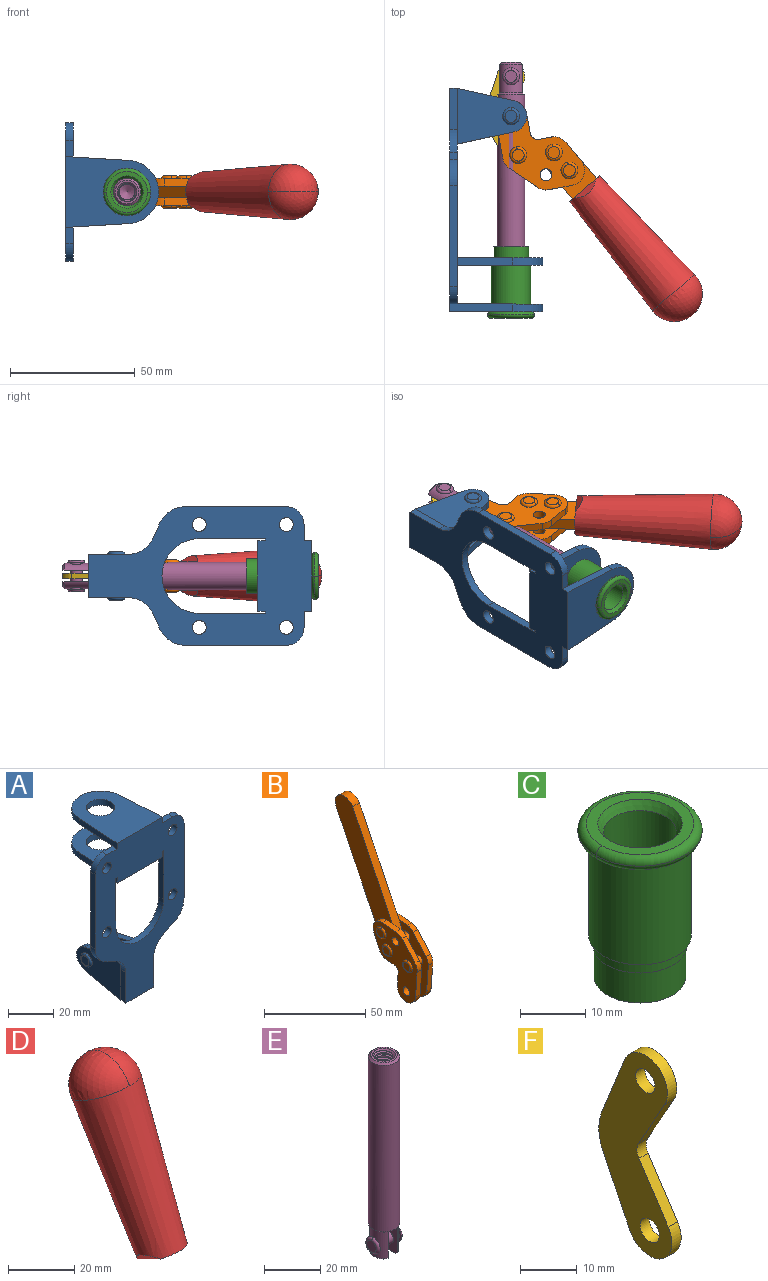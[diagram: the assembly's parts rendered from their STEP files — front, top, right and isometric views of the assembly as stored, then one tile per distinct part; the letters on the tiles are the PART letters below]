
ASSEMBLY  parts=6 mates=6
PART A: 55 faces, bbox 55.7x37.4x89.8 mm
  f0: torus R=2.41mm, axis (-1,0,0), area 15mm2, adj f11,f15,f25
  f1: torus R=2.41mm, axis (-1,0,0), area 15mm2, adj f10,f12,f22
  f2: cylinder r=2.78mm len=5.56mm, axis (0,-1,0), area 54.2mm2, adj f30,f54
  f3: cylinder r=14.99mm len=29.97mm, axis (0,-1,0), area 145.9mm2, adj f30,f49,f53,f54
  f4: cylinder r=2.78mm len=5.56mm, axis (0,-1,0), area 54.2mm2, adj f30,f54
  f5: cylinder r=2.78mm len=5.56mm, axis (0,-1,0), area 54.2mm2, adj f30,f54
  f6: cylinder r=2.78mm len=5.56mm, axis (0,-1,0), area 54.2mm2, adj f30,f54
  f7: cylinder r=6.35mm len=12.7mm, axis (0,0,1), area 123.6mm2, adj f27,f51
  f8: cylinder r=6.35mm len=12.7mm, axis (0,0,-1), area 124.7mm2, adj f21,f35
  f9: cylinder r=2.41mm len=11.18mm, axis (-1,0,0), area 169.4mm2, adj f16,f19
  f10: plane 4.83x4.83mm, normal (1,0,0), area 18.3mm2, adj f1,f12
  f11: plane 4.83x4.83mm, normal (-1,0,0), area 18.3mm2, adj f0,f15
  f12: torus R=2.41mm, axis (-1,0,0), area 15mm2, adj f1,f10,f22
  f13: cylinder r=6.35mm len=12.41mm, axis (1,0,0), area 53.4mm2, adj f18,f19,f22,f23
  f14: cylinder r=6.35mm len=12.41mm, axis (-1,0,0), area 53.4mm2, adj f16,f17,f24,f25
  f15: torus R=2.41mm, axis (-1,0,0), area 15mm2, adj f0,f11,f25
  f16: plane 27.86x22.35mm, normal (1,0,0), area 425.4mm2, adj f9,f14,f17,f24,f30
  f17: plane 22.86x4.97mm, normal (0,0.21,0.98), area 72.5mm2, adj f14,f16,f25,f30
  f18: plane 22.86x4.97mm, normal (0,0.21,0.98), area 72.5mm2, adj f13,f19,f22,f30
  f19: plane 27.86x22.35mm, normal (-1,0,0), area 425.4mm2, adj f9,f13,f18,f23,f30
  f20: cylinder r=12.7mm len=25.35mm, axis (0,0,-1), area 119.8mm2, adj f21,f34,f35,f36
  f21: plane 34.21x28.07mm, normal (0,0,-1), area 702.4mm2, adj f8,f20,f30,f34,f36
  f22: plane 27.96x22.45mm, normal (1,0,0), area 407.2mm2, adj f1,f12,f13,f18,f23,f30,f42,f43
  f23: plane 22.86x4.97mm, normal (0,0.21,-0.98), area 72.5mm2, adj f13,f19,f22,f44
  f24: plane 22.86x4.97mm, normal (0,0.21,-0.98), area 72.5mm2, adj f14,f16,f25,f44
  f25: plane 27.86x22.35mm, normal (-1,0,0), area 407.1mm2, adj f0,f14,f15,f17,f24,f30,f45,f46
  f26: plane 3.1x0.95mm, normal (0,0,-1), area 2.7mm2, adj f30,f49,f50,f54
  f27: plane 34.21x28.07mm, normal (0,0,1), area 702.4mm2, adj f7,f28,f30,f50,f52
  f28: cylinder r=12.7mm len=25.35mm, axis (0,0,1), area 118.8mm2, adj f27,f50,f51,f52
  f29: plane 3.1x0.95mm, normal (0,0,-1), area 2.7mm2, adj f30,f52,f53,f54
  f30: plane 86.54x55.63mm, normal (0,1,0), area 2362.9mm2, adj f2,f3,f4,f5,f6,f16,f17,f18
  f31: plane 40.56x3.1mm, normal (-1,0,0), area 125.7mm2, adj f30,f32,f48,f54
  f32: cylinder r=7.11mm len=7.11mm, axis (0,-1,0), area 34.6mm2, adj f30,f31,f33,f54
  f33: plane 6.67x3.1mm, normal (0,0,1), area 20.4mm2, adj f30,f32,f34,f54
  f34: plane 25.39x3.13mm, normal (-1,0.06,0), area 79.5mm2, adj f20,f21,f33,f35,f54
  f35: plane 37.31x28.45mm, normal (0,0,1), area 789.9mm2, adj f8,f20,f34,f36,f54
  f36: plane 25.39x3.13mm, normal (1,0.06,0), area 79.5mm2, adj f20,f21,f35,f37,f54
  f37: plane 6.67x3.1mm, normal (0,0,1), area 20.4mm2, adj f30,f36,f38,f54
  f38: cylinder r=7.11mm len=7.11mm, axis (0,-1,0), area 34.6mm2, adj f30,f37,f39,f54
  f39: plane 40.56x3.1mm, normal (1,0,0), area 125.7mm2, adj f30,f38,f40,f54
  f40: cylinder r=11.18mm len=10.16mm, axis (0,-1,0), area 39.5mm2, adj f30,f39,f41,f54
  f41: plane 6.09x3.1mm, normal (0.42,0,-0.91), area 20.8mm2, adj f30,f40,f42,f54
  f42: cylinder r=11.18mm len=9.41mm, axis (0,-1,0), area 37.2mm2, adj f22,f30,f41,f43,f54
  f43: plane 16.5x3.1mm, normal (1,0,0), area 51.1mm2, adj f22,f42,f44,f54
  f44: plane 17.37x3.1mm, normal (0,0,-1), area 53.8mm2, adj f23,f24,f30,f43,f45,f54
  f45: plane 16.5x3.1mm, normal (-1,0,0), area 51.1mm2, adj f25,f44,f46,f54
  f46: cylinder r=11.18mm len=9.41mm, axis (0,-1,0), area 37.2mm2, adj f25,f30,f45,f47,f54
  f47: plane 6.09x3.1mm, normal (-0.42,0,-0.91), area 20.8mm2, adj f30,f46,f48,f54
  f48: cylinder r=11.18mm len=10.16mm, axis (0,-1,0), area 39.5mm2, adj f30,f31,f47,f54
  f49: plane 26.54x3.1mm, normal (-1,0,0), area 82.3mm2, adj f3,f26,f30,f54
  f50: plane 25.39x3.1mm, normal (1,0.06,0), area 78.8mm2, adj f26,f27,f28,f51,f54
  f51: plane 37.31x28.45mm, normal (0,0,-1), area 789.9mm2, adj f7,f28,f50,f52,f54
  f52: plane 25.39x3.1mm, normal (-1,0.06,0), area 78.8mm2, adj f27,f28,f29,f51,f54
  f53: plane 26.54x3.1mm, normal (1,0,0), area 82.3mm2, adj f3,f29,f30,f54
  f54: plane 89.66x55.63mm, normal (0,-1,0), area 2678.5mm2, adj f2,f3,f4,f5,f6,f26,f29,f31
PART B: 59 faces, bbox 12.9x60.2x99.6 mm
  f0: torus R=2.39mm, axis (-1,0,0), area 14.9mm2, adj f20,f43,f51
  f1: torus R=2.39mm, axis (-1,0,0), area 14.9mm2, adj f19,f42,f51
  f2: torus R=2.39mm, axis (-1,0,0), area 14.9mm2, adj f18,f35,f51
  f3: torus R=2.39mm, axis (-1,0,0), area 14.9mm2, adj f14,f17,f23
  f4: torus R=2.39mm, axis (-1,0,0), area 14.9mm2, adj f13,f16,f23
  f5: torus R=2.39mm, axis (-1,0,0), area 14.9mm2, adj f12,f15,f23
  f6: cylinder r=2.39mm len=4.78mm, axis (1,0,0), area 46.5mm2, adj f48,f50,f51
  f7: cylinder r=2.39mm len=4.78mm, axis (1,0,0), area 46.5mm2, adj f50,f51
  f8: cylinder r=6.35mm len=12.68mm, axis (1,0,0), area 61.8mm2, adj f38,f39,f50,f51
  f9: cylinder r=2.39mm len=4.78mm, axis (-1,0,0), area 70.5mm2, adj f46,f50
  f10: cylinder r=2.39mm len=4.78mm, axis (-1,0,0), area 46.5mm2, adj f23,f45,f46
  f11: cylinder r=2.39mm len=4.78mm, axis (-1,0,0), area 46.5mm2, adj f23,f46
  f12: plane 4.78x4.78mm, normal (1,0,0), area 17.9mm2, adj f5,f15
  f13: plane 4.78x4.78mm, normal (1,0,0), area 17.9mm2, adj f4,f16
  f14: plane 4.78x4.78mm, normal (1,0,0), area 17.9mm2, adj f3,f17
  f15: torus R=2.39mm, axis (-1,0,0), area 14.9mm2, adj f5,f12,f23
  f16: torus R=2.39mm, axis (-1,0,0), area 14.9mm2, adj f4,f13,f23
  f17: torus R=2.39mm, axis (-1,0,0), area 14.9mm2, adj f3,f14,f23
  f18: plane 4.78x4.78mm, normal (-1,0,0), area 17.9mm2, adj f2,f35
  f19: plane 4.78x4.78mm, normal (-1,0,0), area 17.9mm2, adj f1,f42
  f20: plane 4.78x4.78mm, normal (-1,0,0), area 17.9mm2, adj f0,f43
  f21: plane 2.26x0.2mm, normal (1,0,0), area 0.2mm2, adj f31,f44
  f22: plane 2.26x0.2mm, normal (-1,0,0), area 0.2mm2, adj f41,f44
  f23: plane 39.37x30.77mm, normal (1,0,0), area 565.5mm2, adj f3,f4,f5,f10,f11,f15,f16,f17
  f24: cylinder r=6.1mm len=4.15mm, axis (-1,0,0), area 14.7mm2, adj f23,f25,f32,f46
  f25: plane 10.25x9.01mm, normal (0,-0.75,0.66), area 42.3mm2, adj f23,f24,f26,f46
  f26: cylinder r=6.35mm len=4.64mm, axis (-1,0,0), area 15.6mm2, adj f23,f25,f27,f46
  f27: plane 15.84x3.1mm, normal (0,-1,-0.07), area 49.2mm2, adj f23,f26,f28,f46
  f28: cylinder r=6.35mm len=12.68mm, axis (-1,0,0), area 61.8mm2, adj f23,f27,f29,f46
  f29: plane 8.11x3.1mm, normal (0,1,0.07), area 25.2mm2, adj f23,f28,f30,f46
  f30: cylinder r=3.05mm len=3.25mm, axis (-1,0,0), area 14.8mm2, adj f23,f29,f31,f46
  f31: plane 5.99x3.1mm, normal (0,0.07,-1), area 18.6mm2, adj f21,f23,f30,f44,f46
  f32: plane 9.5x3.1mm, normal (0,-0.07,1), area 29.5mm2, adj f23,f24,f33,f46,f47
  f33: cylinder r=6.1mm len=8.63mm, axis (-1,0,0), area 39.1mm2, adj f23,f32,f34,f47
  f34: plane 8.65x3.96mm, normal (0,0.91,-0.42), area 29.5mm2, adj f23,f33,f44,f47
  f35: torus R=2.39mm, axis (-1,0,0), area 14.9mm2, adj f2,f18,f51
  f36: plane 10.25x9.01mm, normal (0,-0.75,0.66), area 42.3mm2, adj f37,f49,f50,f51
  f37: cylinder r=6.35mm len=4.64mm, axis (1,0,0), area 15.6mm2, adj f36,f38,f50,f51
  f38: plane 15.84x3.1mm, normal (0,-1,-0.07), area 49.2mm2, adj f8,f37,f50,f51
  f39: plane 8.11x3.1mm, normal (0,1,0.07), area 25.2mm2, adj f8,f40,f50,f51
  f40: cylinder r=3.05mm len=3.25mm, axis (1,0,0), area 14.8mm2, adj f39,f41,f50,f51
  f41: plane 5.99x3.1mm, normal (0,0.07,-1), area 18.6mm2, adj f22,f40,f44,f50,f51
  f42: torus R=2.39mm, axis (-1,0,0), area 14.9mm2, adj f1,f19,f51
  f43: torus R=2.39mm, axis (-1,0,0), area 14.9mm2, adj f0,f20,f51
  f44: cylinder r=6.35mm len=12.12mm, axis (-1,0,0), area 128.9mm2, adj f21,f22,f23,f31,f34,f41,f46,f47
  f45: plane 2.65x1.35mm, normal (1,0,0), area 1mm2, adj f10,f55
  f46: plane 39.08x20.42mm, normal (-1,0,0), area 412.5mm2, adj f9,f10,f11,f24,f25,f26,f27,f28
  f47: plane 77.62x39.82mm, normal (1,0,0), area 850mm2, adj f32,f33,f34,f44,f53,f54,f55
  f48: plane 2.65x1.35mm, normal (-1,0,0), area 1mm2, adj f6,f55
  f49: cylinder r=6.1mm len=4.15mm, axis (1,0,0), area 14.7mm2, adj f36,f50,f51,f56
  f50: plane 39.08x20.42mm, normal (1,0,0), area 412.5mm2, adj f6,f7,f8,f9,f36,f37,f38,f39
  f51: plane 39.37x30.77mm, normal (-1,0,0), area 565.5mm2, adj f0,f1,f2,f6,f7,f8,f35,f36
  f52: plane 8.65x3.96mm, normal (0,0.91,-0.42), area 29.5mm2, adj f44,f51,f57,f58
  f53: plane 68.49x33.4mm, normal (0,0.9,-0.44), area 358.1mm2, adj f44,f47,f54,f58
  f54: cylinder r=6.35mm len=12.06mm, axis (1,0,0), area 93.7mm2, adj f47,f53,f55,f58
  f55: plane 68.49x33.4mm, normal (0,-0.9,0.44), area 358.1mm2, adj f44,f45,f46,f47,f48,f50,f54,f58
  f56: plane 9.5x3.1mm, normal (0,-0.07,1), area 29.5mm2, adj f49,f50,f51,f57,f58
  f57: cylinder r=6.1mm len=8.63mm, axis (1,0,0), area 39.1mm2, adj f51,f52,f56,f58
  f58: plane 77.62x39.82mm, normal (-1,0,0), area 850mm2, adj f44,f52,f53,f54,f55,f56,f57
PART C: 15 faces, bbox 20.6x20.6x28.7 mm
  f0: torus R=8.26mm, axis (0,0,1), area 56.8mm2, adj f1,f10,f12
  f1: torus R=8.26mm, axis (0,0,1), area 56.8mm2, adj f0,f6,f13
  f2: cylinder r=5.59mm len=25.91mm, axis (0,0,1), area 909.6mm2, adj f3,f4
  f3: cone r=6.86mm half-angle=45deg, axis (0,0,-1), area 70.2mm2, adj f2,f14
  f4: cone r=6.47mm half-angle=30deg, axis (0,0,1), area 66.7mm2, adj f2,f13
  f5: cylinder r=7.04mm len=14.07mm, axis (0,0,1), area 252.6mm2, adj f11,f14
  f6: torus R=8.26mm, axis (0,0,1), area 56.8mm2, adj f1,f12,f13
  f7: cylinder r=7.16mm len=14.33mm, axis (0,0,1), area 91.5mm2, adj f9,f11
  f8: cylinder r=7.86mm len=18.42mm, axis (0,0,1), area 909.6mm2, adj f9,f10
  f9: plane 15.72x15.72mm, normal (0,0,-1), area 33mm2, adj f7,f8
  f10: plane 16.51x16.51mm, normal (0,0,-1), area 19.9mm2, adj f0,f8,f12
  f11: plane 14.33x14.33mm, normal (0,0,-1), area 5.7mm2, adj f5,f7
  f12: torus R=8.26mm, axis (0,0,1), area 56.8mm2, adj f0,f6,f10
  f13: plane 16.51x16.51mm, normal (0,0,1), area 82.7mm2, adj f1,f4,f6
  f14: plane 14.07x14.07mm, normal (0,0,-1), area 7.8mm2, adj f3,f5
PART D: 11 faces, bbox 22.3x42.6x64.5 mm
  f0: sphere r=11.13mm, area 411.4mm2, adj f1,f8
  f1: cone r=11.11mm half-angle=3.3deg, axis (0,0.44,0.9), area 3251.8mm2, adj f0,f7,f8,f9,f10
  f2: cylinder r=6.16mm len=11.7mm, axis (1,0,0), area 89.5mm2, adj f3,f4,f5,f6
  f3: plane 60.23x36.75mm, normal (-1,0,0), area 763.6mm2, adj f2,f4,f6,f10
  f4: plane 51.37x25.05mm, normal (0,0.9,-0.44), area 264.2mm2, adj f2,f3,f5,f10
  f5: plane 60.23x36.75mm, normal (1,0,0), area 763.6mm2, adj f2,f4,f6,f10
  f6: plane 51.37x25.05mm, normal (0,-0.9,0.44), area 264.2mm2, adj f2,f3,f5,f10
  f7: plane 9.95x5.95mm, normal (0.71,-0.31,-0.64), area 25.8mm2, adj f1,f10
  f8: sphere r=11.13mm, area 411.4mm2, adj f0,f1
  f9: plane 9.95x5.95mm, normal (-0.71,-0.31,-0.64), area 25.8mm2, adj f1,f10
  f10: plane 14.27x11.38mm, normal (0,-0.44,-0.9), area 106.7mm2, adj f1,f3,f4,f5,f6,f7,f9
PART E: 48 faces, bbox 12.6x11.1x86.1 mm
  f0: torus R=2.41mm, axis (-1,0,0), area 15mm2, adj f30,f32,f34
  f1: torus R=2.41mm, axis (-1,0,0), area 15mm2, adj f29,f31,f33
  f2: cylinder r=5.54mm len=72.39mm, axis (0,0,1), area 2518.5mm2, adj f3,f4,f42,f43
  f3: cone r=5.54mm half-angle=45deg, axis (0,0,1), area 7.6mm2, adj f2,f5,f41
  f4: cone r=5.54mm half-angle=45deg, axis (0,0,-1), area 34.9mm2, adj f2,f39
  f5: cylinder r=5.08mm len=11.48mm, axis (0,0,1), area 108.3mm2, adj f3,f7,f8,f41
  f6: cylinder r=2.41mm len=4.83mm, axis (-1,0,0), area 71.2mm2, adj f40,f41
  f7: cylinder r=2.41mm len=4.83mm, axis (-1,0,0), area 7.6mm2, adj f5,f34
  f8: cone r=5.08mm half-angle=45deg, axis (0,0,1), area 10.6mm2, adj f5,f37,f41
  f9: cone r=3.98mm half-angle=45deg, axis (0,0,1), area 17.6mm2, adj f27,f39,f45,f46,f47
  f10: cylinder r=2.41mm len=4.83mm, axis (-1,0,0), area 7.6mm2, adj f33,f38
  f11: cylinder r=3.2mm len=6.4mm, axis (0,0,1), area 78.4mm2, adj f12,f28,f44,f45,f47
  f12: cylinder r=3.2mm len=6.4mm, axis (0,0,1), area 10.5mm2, adj f11,f13,f45,f47
  f13: cylinder r=3.2mm len=6.4mm, axis (0,0,1), area 10.5mm2, adj f12,f14,f45,f47
  f14: cylinder r=3.2mm len=6.4mm, axis (0,0,1), area 10.5mm2, adj f13,f15,f45,f47
  f15: cylinder r=3.2mm len=6.4mm, axis (0,0,1), area 10.5mm2, adj f14,f16,f45,f47
  f16: cylinder r=3.2mm len=6.4mm, axis (0,0,1), area 10.5mm2, adj f15,f17,f45,f47
  f17: cylinder r=3.2mm len=6.4mm, axis (0,0,1), area 10.5mm2, adj f16,f18,f45,f47
  f18: cylinder r=3.2mm len=6.4mm, axis (0,0,1), area 10.5mm2, adj f17,f19,f45,f47
  f19: cylinder r=3.2mm len=6.4mm, axis (0,0,1), area 10.5mm2, adj f18,f20,f45,f47
  f20: cylinder r=3.2mm len=6.4mm, axis (0,0,1), area 10.5mm2, adj f19,f21,f45,f47
  f21: cylinder r=3.2mm len=6.4mm, axis (0,0,1), area 10.5mm2, adj f20,f22,f45,f47
  f22: cylinder r=3.2mm len=6.4mm, axis (0,0,1), area 10.5mm2, adj f21,f23,f45,f47
  f23: cylinder r=3.2mm len=6.4mm, axis (0,0,1), area 10.5mm2, adj f22,f24,f45,f47
  f24: cylinder r=3.2mm len=6.4mm, axis (0,0,1), area 10.5mm2, adj f23,f25,f45,f47
  f25: cylinder r=3.2mm len=6.4mm, axis (0,0,1), area 10.5mm2, adj f24,f26,f45,f47
  f26: cylinder r=3.2mm len=6.4mm, axis (0,0,1), area 10.5mm2, adj f25,f27,f45,f47
  f27: cylinder r=3.2mm len=6.4mm, axis (0,0,1), area 7.4mm2, adj f9,f26,f45,f47
  f28: cone r=3.2mm half-angle=60deg, axis (0,0,1), area 37.2mm2, adj f11
  f29: plane 4.83x4.83mm, normal (-1,0,0), area 18.3mm2, adj f1,f31
  f30: plane 4.83x4.83mm, normal (1,0,0), area 18.3mm2, adj f0,f32
  f31: torus R=2.41mm, axis (-1,0,0), area 15mm2, adj f1,f29,f33
  f32: torus R=2.41mm, axis (-1,0,0), area 15mm2, adj f0,f30,f34
  f33: plane 6.83x6.83mm, normal (1,0,0), area 18.3mm2, adj f1,f10,f31
  f34: plane 6.83x6.83mm, normal (-1,0,0), area 18.3mm2, adj f0,f7,f32
  f35: cone r=5.08mm half-angle=45deg, axis (0,0,1), area 10.6mm2, adj f36,f38,f40
  f36: plane 7.25x1.97mm, normal (0,0,-1), area 10mm2, adj f35,f40
  f37: plane 7.25x1.97mm, normal (0,0,-1), area 10mm2, adj f8,f41
  f38: cylinder r=5.08mm len=11.48mm, axis (0,0,1), area 108.3mm2, adj f10,f35,f40,f42
  f39: plane 9.55x9.55mm, normal (0,0,1), area 22mm2, adj f4,f9
  f40: plane 12.76x10.09mm, normal (1,0,0), area 95.7mm2, adj f6,f35,f36,f38,f42,f43
  f41: plane 12.76x10.09mm, normal (-1,0,0), area 95.7mm2, adj f3,f5,f6,f8,f37,f43
  f42: cone r=5.54mm half-angle=45deg, axis (0,0,1), area 7.6mm2, adj f2,f38,f40
  f43: plane 11.07x4.7mm, normal (0,0,-1), area 50.4mm2, adj f2,f40,f41
  f44: plane 0.89x0.62mm, normal (-1,0,0), area 0.3mm2, adj f11,f45,f46,f47
  f45: bspline ~24.8x7.63mm, area 266.6mm2, adj f9,f11,f12,f13,f14,f15,f16,f17
  f46: bspline ~24.87x7.63mm, area 73.6mm2, adj f9,f44,f45,f47
  f47: bspline ~24.98x7.63mm, area 272.5mm2, adj f9,f11,f12,f13,f14,f15,f16,f17
PART F: 12 faces, bbox 2.3x18.2x42.8 mm
  f0: cylinder r=2.4mm len=4.8mm, axis (1,0,0), area 34.9mm2, adj f4,f11
  f1: cylinder r=10.41mm len=8.47mm, axis (1,0,0), area 20.2mm2, adj f4,f9,f10,f11
  f2: cylinder r=3.05mm len=3.16mm, axis (1,0,0), area 7.7mm2, adj f4,f6,f7,f11
  f3: cylinder r=2.4mm len=4.8mm, axis (1,0,0), area 34.9mm2, adj f4,f11
  f4: plane 42.81x18.23mm, normal (-1,0,0), area 414.1mm2, adj f0,f1,f2,f3,f5,f6,f7,f8
  f5: cylinder r=5.54mm len=10.67mm, axis (1,0,0), area 41.8mm2, adj f4,f6,f10,f11
  f6: plane 11.66x6.53mm, normal (0,-0.87,-0.49), area 30.9mm2, adj f2,f4,f5,f11
  f7: plane 11.17x7.33mm, normal (0,-0.84,0.55), area 30.9mm2, adj f2,f4,f8,f11
  f8: cylinder r=5.54mm len=10.51mm, axis (1,0,0), area 41.8mm2, adj f4,f7,f9,f11
  f9: plane 13.67x6.67mm, normal (0,0.9,-0.44), area 35.1mm2, adj f1,f4,f8,f11
  f10: plane 14.1x5.7mm, normal (0,0.93,0.37), area 35.1mm2, adj f1,f4,f5,f11
  f11: plane 42.81x18.23mm, normal (1,0,0), area 414.1mm2, adj f0,f1,f2,f3,f5,f6,f7,f8
PLACE A rot(axis=(0.58,0.58,-0.58),120deg) t=(0,0,0)mm fixed
PLACE B rot(axis=(0.52,0.67,-0.52),112deg) t=(8.81,-5.14,0)mm
PLACE C rot(axis=(1,0,0),90deg) t=(24.61,0,-24.61)mm
PLACE D rot(axis=(0.52,0.67,-0.52),112deg) t=(8.81,-5.14,0.04)mm
PLACE E rot(axis=(0.58,-0.58,0.58),120deg) t=(49.23,63.58,0)mm
PLACE F rot(axis=(-0.59,0.56,0.59),121.9deg) t=(50.06,34.04,0)mm
MATE revolute F.f5 <-> E.f6  axis (0,0,-1) through (24.61,48.1,0)mm
MATE slider A.f7 <-> C.f2  axis (0,-1,0) through (24.61,-46.39,0)mm
MATE revolute B.f7 <-> A.f0  axis (0,0,1) through (24.61,32.09,0)mm
MATE fastened D.f2 <-> B.f54  axis (0,0,-1) through (91.3,-40.39,2.35)mm
MATE revolute F.f3 <-> B.f4  axis (0,0,-1) through (27.5,16.48,0)mm
MATE slider E.f2 <-> C.f2  axis (0,-1,0) through (24.61,4.79,0)mm
